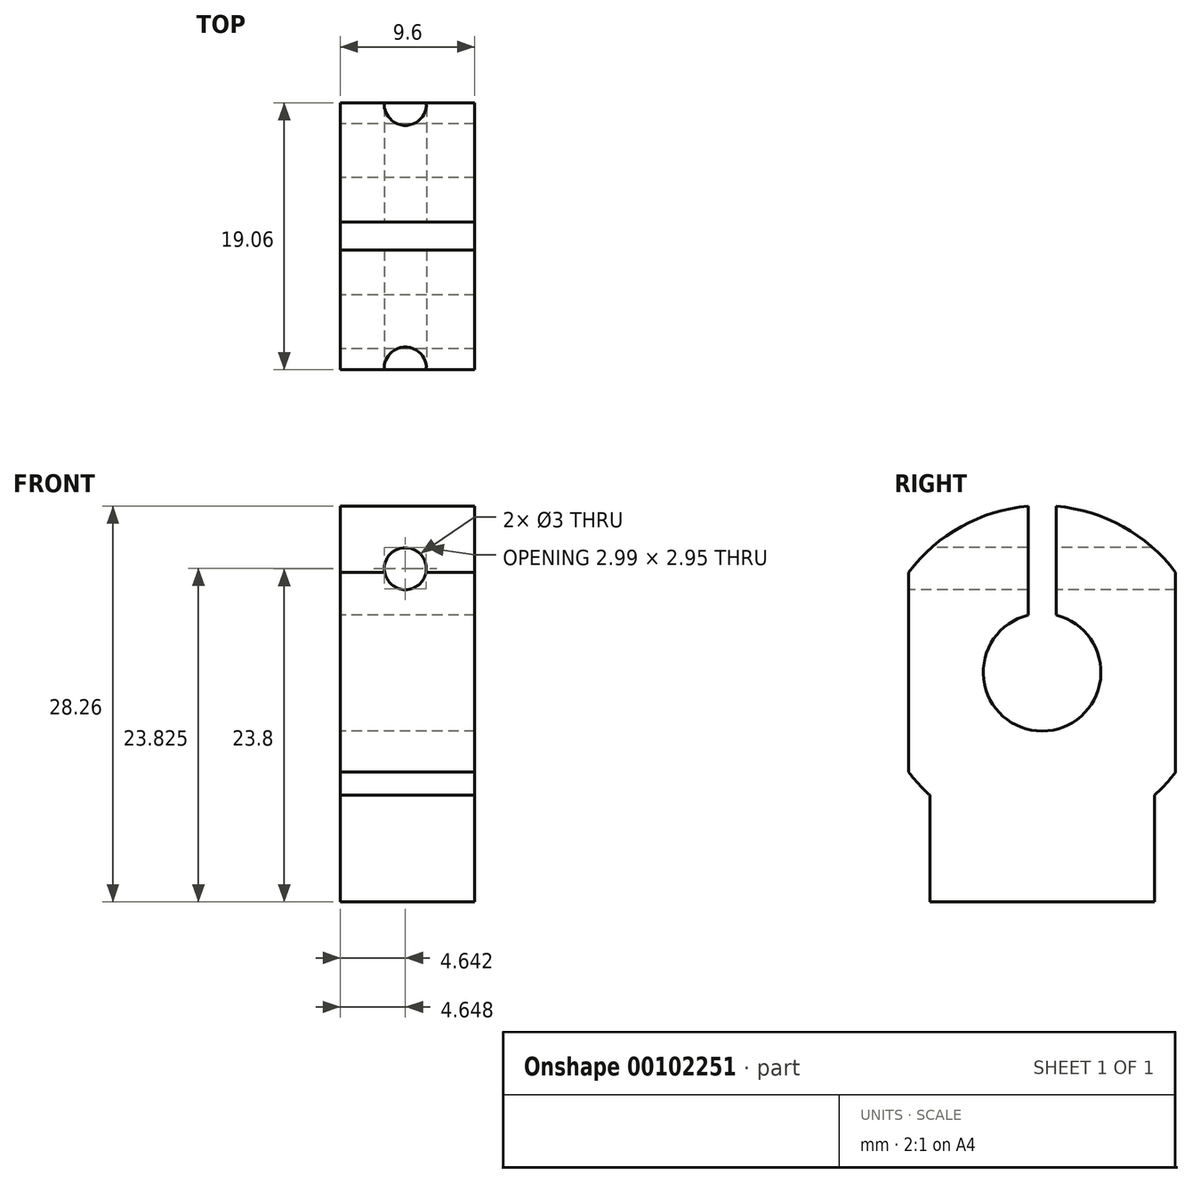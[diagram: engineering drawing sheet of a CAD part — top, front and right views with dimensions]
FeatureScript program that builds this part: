
annotation { "Feature Type Name" : "Feature", "Feature Type Description" : "" }
export const myFeature = defineFeature(function(context is Context, id is Id, definition is map)
    precondition{}
    {
        {
            var Q0;
            Q0=qCreatedBy(makeId("Right.planeOp"),FACE);
            var sketch = newSketch(context, id + "F0", { "sketchPlane" : qUnion([Q0])});
            skArc(sketch, "E0", {"start": v(-9.52, -7.13) * mm, "mid": v(0, -11.9) * mm, "end": v(9.53, -7.13) * mm});
            skLineSegment(sketch, "E1", {"start": v(0, 11.9) * mm, "end": v(0, -16.4) * mm, "construction": true});
            skLineSegment(sketch, "E2.0", {"start": v(-9.52, 7.13) * mm, "end": v(-9.52, -7.13) * mm});
            skLineSegment(sketch, "E3.0", {"start": v(9.53, 7.13) * mm, "end": v(9.53, -7.13) * mm});
            skLineSegment(sketch, "E4.0", {"start": v(-8.02, -8.79) * mm, "end": v(-8.02, -16.4) * mm});
            skLineSegment(sketch, "E5.0", {"start": v(8.03, -8.79) * mm, "end": v(8.03, -16.4) * mm});
            skLineSegment(sketch, "E6", {"start": v(-8.02, -16.4) * mm, "end": v(8.03, -16.4) * mm});
            skArc(sketch, "E7.trimOffspring", {"start": v(9.53, 7.13) * mm, "mid": v(0, 11.9) * mm, "end": v(-9.52, 7.13) * mm});
            skCircle(sketch, "E8", {"center": v(0, 0) * mm, "radius": 4.2 * mm});
            skSolve(sketch);
        }
        {
            var Q0;
            Q0 = qSketchRegion(id + "F0", true);
            extrude(context, id + "F1", {"entities" : qUnion([Q0]), "depth" : 9.6 * mm});
        }
        {
            var Q0;
            Q0=makeQuery(id+"F1.opExtrude","SWEPT_FACE",FACE,{"disambiguationData":[OSD([sQuery(id+"F0.wireOp",EDGE,"E2.0")])]});
            var sketch = newSketch(context, id + "F2", { "sketchPlane" : qUnion([Q0])});
            skLineSegment(sketch, "E9", {"start": v(4.64, 9.44) * mm, "end": v(4.64, -19) * mm, "construction": true});
            skCircle(sketch, "E10", {"center": v(4.64, 7.4) * mm, "radius": 1.5 * mm});
            skSolve(sketch);
        }
        {
            var Q0;
            Q0 = qSketchRegion(id + "F2", true);
            extrude(context, id + "F3", {"entities" : qUnion([Q0]), "operationType" : NewBodyOperationType.REMOVE, "endBound" : BoundingType.THROUGH_ALL, "oppositeDirection" : true, "depth" : 25 * mm});
        }
        {
            var Q0;
            Q0=qCreatedBy(makeId("Top.planeOp"),FACE);
            var sketch = newSketch(context, id + "F4", { "sketchPlane" : qUnion([Q0])});
            skLineSegment(sketch, "E11", {"start": v(0, 0) * mm, "end": v(9.64, 0) * mm, "construction": true});
            skLineSegment(sketch, "E12.0", {"start": v(0, -1) * mm, "end": v(9.64, -1) * mm});
            skLineSegment(sketch, "E13.0", {"start": v(0, 1) * mm, "end": v(9.64, 1) * mm});
            skLineSegment(sketch, "E14", {"start": v(0, 1) * mm, "end": v(0, -1) * mm});
            skLineSegment(sketch, "E15", {"start": v(9.64, 1) * mm, "end": v(9.64, -1) * mm});
            skPoint(sketch, "E16.orphan", {"position": v(17.28, -1) * mm});
            skSolve(sketch);
        }
        {
            var Q0;
            Q0 = qSketchRegion(id + "F4", true);
            extrude(context, id + "F5", {"entities" : qUnion([Q0]), "operationType" : NewBodyOperationType.REMOVE, "endBound" : BoundingType.THROUGH_ALL, "depth" : 25 * mm});
        }
    });
